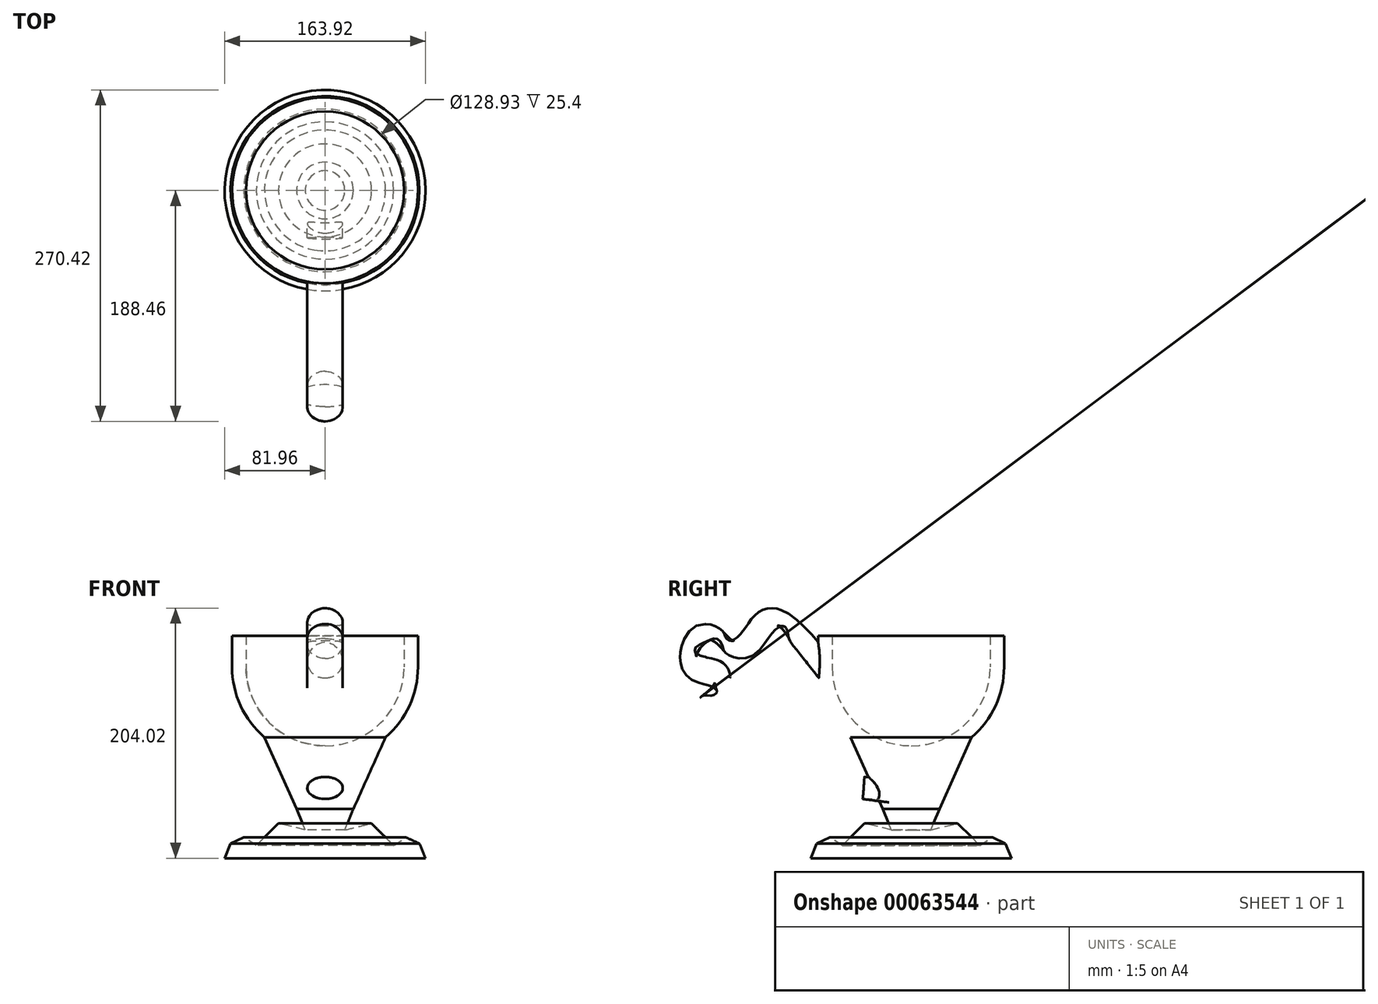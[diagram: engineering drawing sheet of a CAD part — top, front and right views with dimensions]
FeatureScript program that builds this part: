
annotation { "Feature Type Name" : "Feature", "Feature Type Description" : "" }
export const myFeature = defineFeature(function(context is Context, id is Id, definition is map)
    precondition{}
    {
        {
            var Q0;
            Q0=qCreatedBy(makeId("Front.planeOp"),FACE);
            var sketch = newSketch(context, id + "F0", { "sketchPlane" : qUnion([Q0])});
            skPoint(sketch, "E0.center.orphan", {"position": v(1.85, 0) * mm});
            skArc(sketch, "E1", {"start": v(-75.85, 0) * mm, "mid": v(-68.91, -31.7) * mm, "end": v(-49.36, -57.6) * mm});
            skArc(sketch, "E2", {"start": v(-64.46, 0) * mm, "mid": v(-45.58, -45.58) * mm, "end": v(0, -64.46) * mm});
            skLineSegment(sketch, "E3", {"start": v(-75.85, 0) * mm, "end": v(-64.46, 0) * mm});
            skLineSegment(sketch, "E4", {"start": v(0, -64.46) * mm, "end": v(0, -156.18) * mm});
            skLineSegment(sketch, "E5", {"start": v(0, -156.18) * mm, "end": v(-81.96, -156.18) * mm});
            skLineSegment(sketch, "E6", {"start": v(-81.96, -156.18) * mm, "end": v(-77.02, -144.25) * mm});
            skLineSegment(sketch, "E7", {"start": v(-77.02, -144.25) * mm, "end": v(-66.32, -139.31) * mm});
            skLineSegment(sketch, "E8", {"start": v(-66.32, -139.31) * mm, "end": v(-56.04, -145.9) * mm});
            skLineSegment(sketch, "E9", {"start": v(-56.04, -145.9) * mm, "end": v(-37.93, -127.79) * mm});
            skLineSegment(sketch, "E10", {"start": v(-37.93, -127.79) * mm, "end": v(-16.13, -133.14) * mm});
            skLineSegment(sketch, "E11", {"start": v(-16.13, -133.14) * mm, "end": v(-23.12, -115.86) * mm});
            skLineSegment(sketch, "E12", {"start": v(-23.12, -115.86) * mm, "end": v(-49.36, -57.6) * mm});
            skSolve(sketch);
        }
        {
            var Q0;
            Q0 = qSketchRegion(id + "F0", true);
            var Q1;
            Q1=sQuery(id+"F0.wireOp",EDGE,"E4");
            revolve(context, id + "F1", {"entities" : qUnion([Q0]), "axis" : qUnion([Q1]), "revolveType" : RevolveType.FULL});
        }
        {
            var Q0;
            Q0=makeQuery(id+"F1.opRevolve","SWEPT_FACE",FACE,{"disambiguationData":[OSD([sQuery(id+"F0.wireOp",EDGE,"E3")])]});
            extrude(context, id + "F2", {"entities" : qUnion([Q0]), "operationType" : NewBodyOperationType.ADD, "depth" : 25.4 * mm});
        }
        {
            var Q0;
            Q0=qCreatedBy(makeId("Front.planeOp"),FACE);
            cPlane(context, id + "F3", {"entities" : qUnion([Q0]), "cplaneType" : CPlaneType.OFFSET, "offset" : 71.12 * mm, "width" : 152.4 * mm, "height" : 152.4 * mm});
        }
        {
            var Q0;
            Q0=qCreatedBy(id+"F3.planeOp",FACE);
            var sketch = newSketch(context, id + "F4", { "sketchPlane" : qUnion([Q0])});
            skCircle(sketch, "E13", {"center": v(0, 0) * mm, "radius": 14.4 * mm});
            skSolve(sketch);
        }
        {
            var Q0;
            Q0=qCreatedBy(makeId("Right.planeOp"),FACE);
            var sketch = newSketch(context, id + "F5", { "sketchPlane" : qUnion([Q0])});
            skFitSpline(sketch, "E14", {"points": [v(-71, 0) * mm, v(-114.92, 36.13) * mm, v(-139, 18.04) * mm, v(-167.9, 23.77) * mm, v(-176.12, 3.29) * mm, v(-159.1, -10.45) * mm, v(-162.65, -32.98) * mm, v(-115.57, -43.85) * mm, v(-111.7, -74.37) * mm, v(-38.7, -98.95) * mm], "startDerivative": vector(-369.47, 461.79) * mm, "endDerivative": vector(643.83, -84.97) * mm});
            skLineSegment(sketch, "E15", {"start": v(-38.7, -98.95) * mm, "end": v(-22.51, -98.95) * mm});
            skSolve(sketch);
        }
        {
            var Q0;
            Q0 = qSketchRegion(id + "F4", true);
            var Q1;
            Q1 = qConstructionFilter(qBodyType(qCreatedBy(id + "F5" ,EDGE), BodyType.WIRE), ConstructionObject.NO);
            sweep(context, id + "F6", {"operationType" : NewBodyOperationType.ADD, "profiles" : qUnion([Q0]), "path" : qUnion([Q1])});
        }
    });
